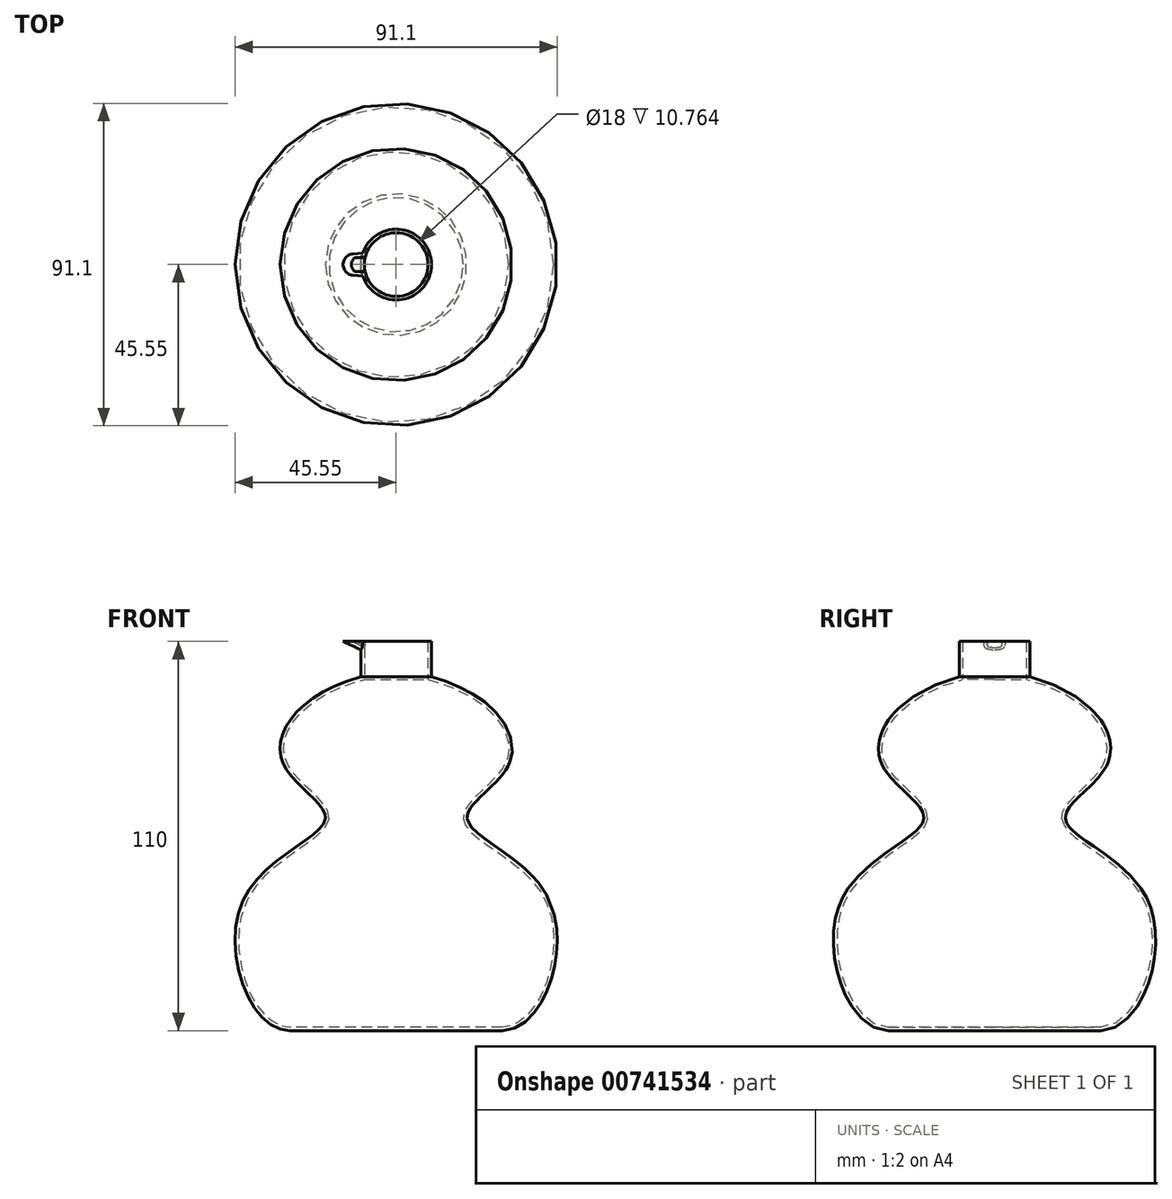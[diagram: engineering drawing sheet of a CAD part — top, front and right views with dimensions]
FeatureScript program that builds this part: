
annotation { "Feature Type Name" : "Feature", "Feature Type Description" : "" }
export const myFeature = defineFeature(function(context is Context, id is Id, definition is map)
    precondition{}
    {
        {
            var Q0;
            Q0=qCreatedBy(makeId("Front.planeOp"),FACE);
            var sketch = newSketch(context, id + "F0", { "sketchPlane" : qUnion([Q0])});
            skLineSegment(sketch, "E0", {"start": v(30, -60) * mm, "end": v(0, -60) * mm});
            skLineSegment(sketch, "E1", {"start": v(0, -60) * mm, "end": v(0, 0) * mm});
            skLineSegment(sketch, "E2", {"start": v(0, 0) * mm, "end": v(20, 0) * mm});
            skLineSegment(sketch, "E3", {"start": v(0, 0) * mm, "end": v(0, 50) * mm});
            skLineSegment(sketch, "E4", {"start": v(0, 50) * mm, "end": v(10, 50) * mm});
            skLineSegment(sketch, "E5", {"start": v(10, 50) * mm, "end": v(10, 40) * mm});
            skFitSpline(sketch, "E6", {"points": [v(10, 40) * mm, v(31.96, 15.53) * mm, v(20, 0) * mm, v(43.5, -23.6) * mm, v(30, -60) * mm], "startDerivative": vector(206, -56.12) * mm, "endDerivative": vector(-123.6, 0) * mm});
            skSolve(sketch);
        }
        {
            var Q0;
            Q0 = qSketchRegion(id + "F0", true);
            var Q1;
            Q1=sQuery(id+"F0.wireOp",EDGE,"E1");
            revolve(context, id + "F1", {"surfaceOperationType" : NewSurfaceOperationType.NEW, "entities" : qUnion([Q0]), "axis" : qUnion([Q1]), "revolveType" : RevolveType.FULL});
        }
        {
            var Q0;
            Q0=makeQuery(id+"F1.opRevolve","SWEPT_FACE",FACE,{"disambiguationData":[OSD([sQuery(id+"F0.wireOp",EDGE,"E4")])]});
            var sketch = newSketch(context, id + "F2", { "sketchPlane" : qUnion([Q0])});
            skArc(sketch, "E7", {"start": v(-15, 0) * mm, "mid": v(-14.2, -2.03) * mm, "end": v(-12.25, -2.99) * mm});
            skLineSegment(sketch, "E8", {"start": v(0, 0) * mm, "end": v(0, -4) * mm});
            skLineSegment(sketch, "E9", {"start": v(0, -4) * mm, "end": v(-12.25, -2.99) * mm});
            skArc(sketch, "E10.MirrorCS", {"start": v(-15, 0) * mm, "mid": v(-14.2, 2.03) * mm, "end": v(-12.25, 2.99) * mm});
            skLineSegment(sketch, "E11.MirrorCS", {"start": v(0, 4) * mm, "end": v(-12.25, 2.99) * mm});
            skLineSegment(sketch, "E12.MirrorCS", {"start": v(0, 0) * mm, "end": v(0, 4) * mm});
            skSolve(sketch);
        }
        {
            var Q0;
            Q0=qCreatedBy(makeId("Front.planeOp"),FACE);
            var sketch = newSketch(context, id + "F3", { "sketchPlane" : qUnion([Q0])});
            skLineSegment(sketch, "E13", {"start": v(0, 50) * mm, "end": v(8.16, 46.2) * mm});
            skSolve(sketch);
        }
        {
            var Q0;
            Q0 = qSketchRegion(id + "F2", true);
            var Q1;
            Q1 = qConstructionFilter(qBodyType(qCreatedBy(id + "F3" ,EDGE), BodyType.WIRE), ConstructionObject.NO);
            sweep(context, id + "F4", {"operationType" : NewBodyOperationType.ADD, "profiles" : qUnion([Q0]), "path" : qUnion([Q1])});
        }
        {
            var Q0;
            Q0=makeQuery(id+"F4.boolean.opBoolean","MERGE",FACE,{"derivedFrom":[makeQuery(id+"F1.opRevolve","SWEPT_FACE",FACE,{"disambiguationData":[OSD([sQuery(id+"F0.wireOp",EDGE,"E4")])]}),makeQuery(id+"F4.opSweep","CAP_FACE",FACE,{"disambiguationData":[OSD([sQuery(id+"F2.wireOp",EDGE,"E7"),sQuery(id+"F2.wireOp",EDGE,"E8"),sQuery(id+"F2.wireOp",EDGE,"E9"),sQuery(id+"F2.wireOp",EDGE,"E10.MirrorCS"),sQuery(id+"F2.wireOp",EDGE,"E11.MirrorCS"),sQuery(id+"F2.wireOp",EDGE,"E12.MirrorCS"),sQuery(id+"F3.wireOp",VERTEX,"E13.start")])],"isStart":true})]});
            shell(context, id + "F5", {"entities" : qUnion([Q0]), "thickness" : 1 * mm});
        }
    });
